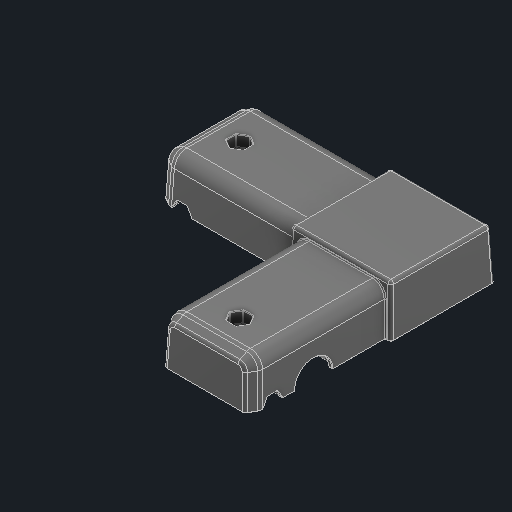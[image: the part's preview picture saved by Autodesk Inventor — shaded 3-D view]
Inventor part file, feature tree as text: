
AUTODESK INVENTOR PART (.ipt)
format: ipt  version: 2025 (Build 290162000, 162)  size: 5,283,840 bytes
history: native  units: in
note: dims shown in document units (in); Inventor stores cm internally (conversion verified against a paired STEP export)
features: fillet x1
ambient origin geometry x8: Origin, YZ Plane, XZ Plane, XY Plane, X Axis, Y Axis, Z Axis, Center Point
bodies: Solid1 (feature_tree)
feature tree (1):
  fillet  "Fillet54"  [1 undecoded]
note: 1 required parameter value undecoded (feature->parameter linkage not recoverable at this tier; creation-order binding heuristic only, values carry confidence <= 0.55)
